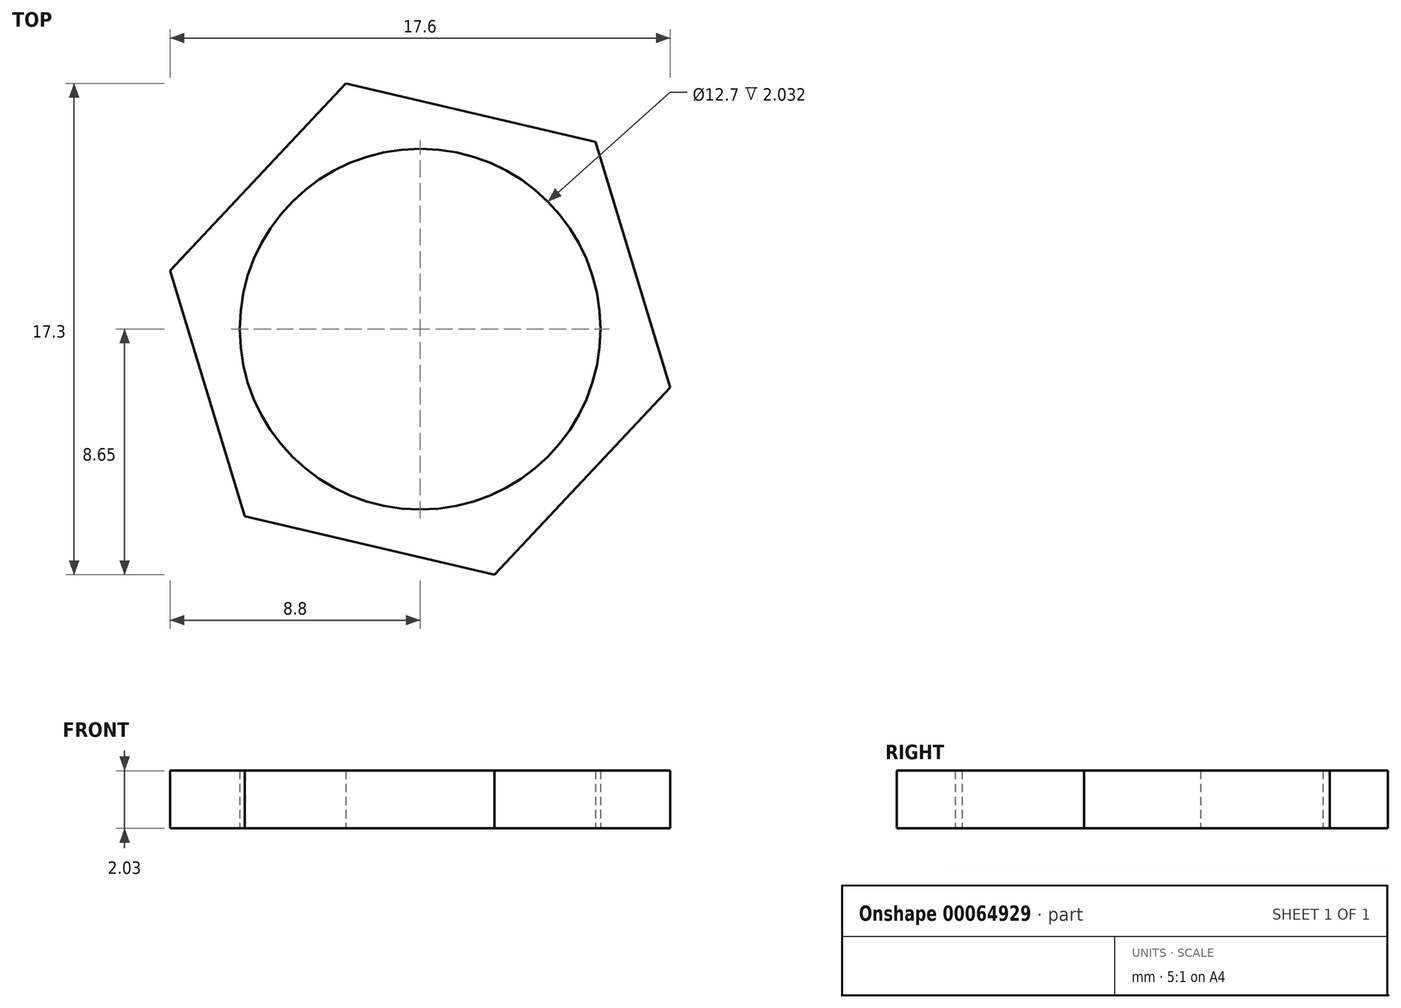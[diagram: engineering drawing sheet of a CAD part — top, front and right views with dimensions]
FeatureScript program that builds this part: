
annotation { "Feature Type Name" : "Feature", "Feature Type Description" : "" }
export const myFeature = defineFeature(function(context is Context, id is Id, definition is map)
    precondition{}
    {
        {
            var Q0;
            Q0=qCreatedBy(makeId("Top.planeOp"),FACE);
            var sketch = newSketch(context, id + "F0", { "sketchPlane" : qUnion([Q0])});
            skCircle(sketch, "E0", {"center": v(0, 0) * mm, "radius": 6.35 * mm});
            skCircle(sketch, "E1.cCircle", {"center": v(0, 0) * mm, "radius": 7.82 * mm, "construction": true});
            skLineSegment(sketch, "E1.0", {"start": v(8.8, -2.05) * mm, "end": v(2.62, -8.65) * mm});
            skLineSegment(sketch, "E1.1", {"start": v(2.62, -8.65) * mm, "end": v(-6.18, -6.6) * mm});
            skLineSegment(sketch, "E1.2", {"start": v(-6.18, -6.6) * mm, "end": v(-8.8, 2.05) * mm});
            skLineSegment(sketch, "E1.3", {"start": v(-8.8, 2.05) * mm, "end": v(-2.62, 8.65) * mm});
            skLineSegment(sketch, "E1.4", {"start": v(-2.62, 8.65) * mm, "end": v(6.18, 6.6) * mm});
            skLineSegment(sketch, "E1.5", {"start": v(6.18, 6.6) * mm, "end": v(8.8, -2.05) * mm});
            skPoint(sketch, "E1.0.midPoint", {"position": v(5.7, -5.35) * mm});
            skSolve(sketch);
        }
        {
            var Q0;
            Q0=makeQuery(id+"F0.imprint","IMPRINT",FACE,{"disambiguationData":[TD([[makeQuery(id+"F0.imprint","IMPRINT",EDGE,{"derivedFrom":sQuery(id+"F0.wireOp",EDGE,"E0")}),-1.0]])]});
            extrude(context, id + "F1", {"entities" : qUnion([Q0]), "depth" : 2.03 * mm});
        }
    });
